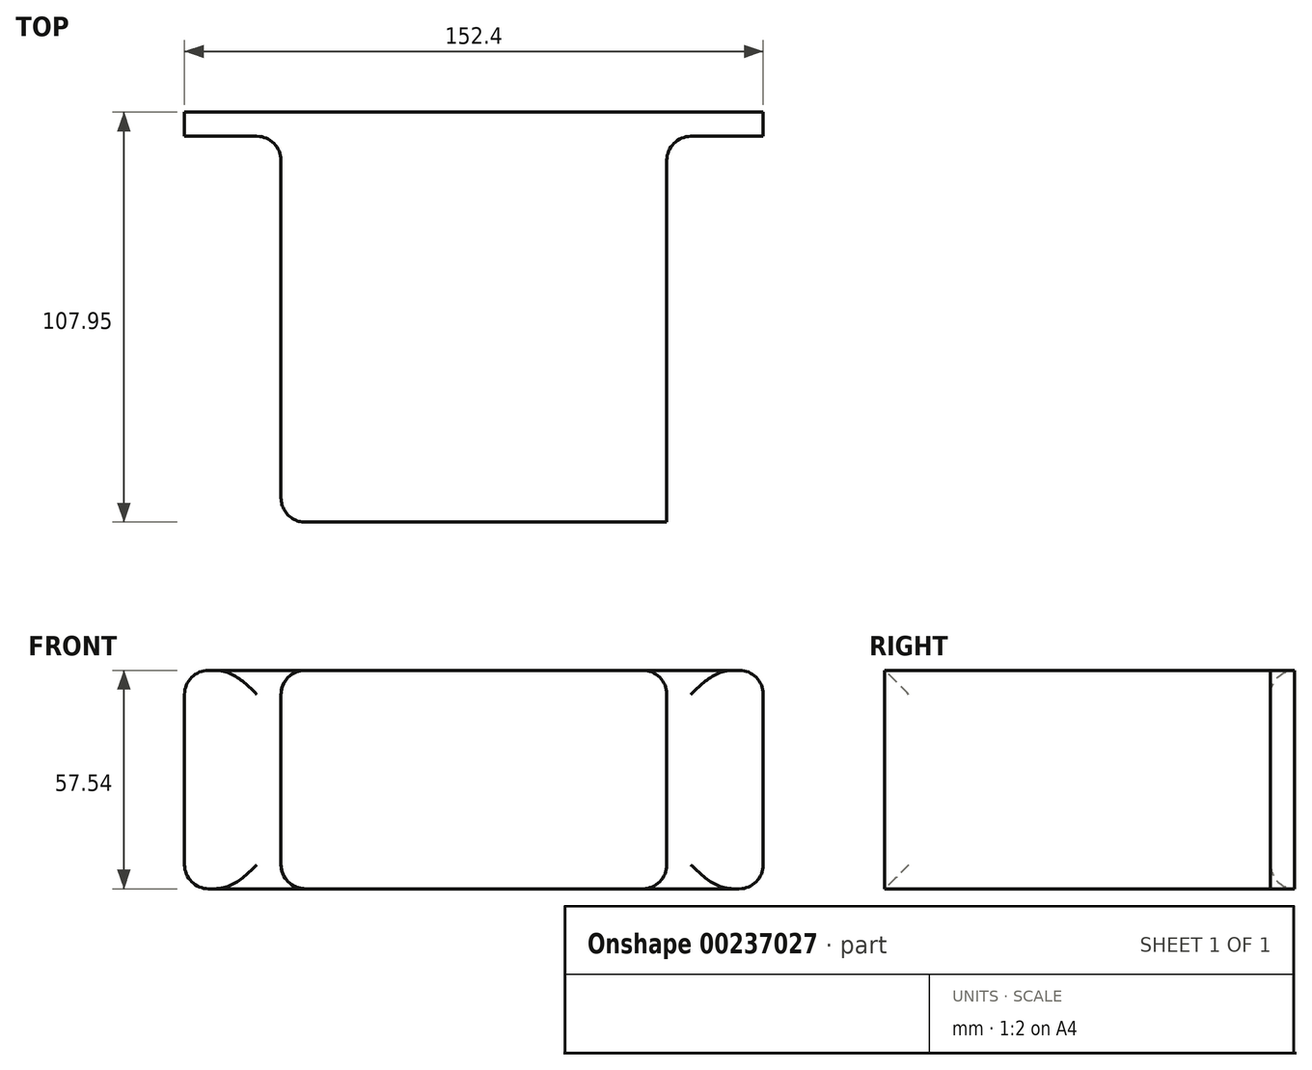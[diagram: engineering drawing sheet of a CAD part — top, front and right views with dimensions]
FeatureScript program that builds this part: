
annotation { "Feature Type Name" : "Feature", "Feature Type Description" : "" }
export const myFeature = defineFeature(function(context is Context, id is Id, definition is map)
    precondition{}
    {
        {
            var Q0;
            Q0=qCreatedBy(makeId("Front.planeOp"),FACE);
            var sketch = newSketch(context, id + "F0", { "sketchPlane" : qUnion([Q0])});
            skLineSegment(sketch, "E0.bottom", {"start": v(76.2, 28.77) * mm, "end": v(-76.2, 28.77) * mm});
            skLineSegment(sketch, "E0.top", {"start": v(76.2, -28.77) * mm, "end": v(-76.2, -28.77) * mm});
            skLineSegment(sketch, "E0.left", {"start": v(76.2, 28.77) * mm, "end": v(76.2, -28.77) * mm});
            skLineSegment(sketch, "E0.right", {"start": v(-76.2, 28.77) * mm, "end": v(-76.2, -28.77) * mm});
            skPoint(sketch, "E0.middle", {"position": v(0, 0) * mm});
            skSolve(sketch);
        }
        {
            var Q0;
            Q0=makeQuery(id+"F0.imprint","IMPRINT",FACE,{"disambiguationData":[TD([[makeQuery(id+"F0.imprint","IMPRINT",EDGE,{"derivedFrom":sQuery(id+"F0.wireOp",EDGE,"E0.bottom")}),1.0]])]});
            extrude(context, id + "F1", {"entities" : qUnion([Q0]), "depth" : 6.35 * mm});
        }
        {
            var Q0;
            Q0=makeQuery(id+"F1.opExtrude","CAP_FACE",FACE,{"disambiguationData":[OSD([sQuery(id+"F0.wireOp",EDGE,"E0.bottom"),sQuery(id+"F0.wireOp",EDGE,"E0.top"),sQuery(id+"F0.wireOp",EDGE,"E0.left"),sQuery(id+"F0.wireOp",EDGE,"E0.right")])],"isStart":false});
            var sketch = newSketch(context, id + "F2", { "sketchPlane" : qUnion([Q0])});
            skLineSegment(sketch, "E1.bottom", {"start": v(50.8, 28.77) * mm, "end": v(-50.8, 28.77) * mm});
            skLineSegment(sketch, "E1.top", {"start": v(50.8, -28.77) * mm, "end": v(-50.8, -28.77) * mm});
            skLineSegment(sketch, "E1.left", {"start": v(50.8, 28.77) * mm, "end": v(50.8, -28.77) * mm});
            skLineSegment(sketch, "E1.right", {"start": v(-50.8, 28.77) * mm, "end": v(-50.8, -28.77) * mm});
            skPoint(sketch, "E1.middle", {"position": v(0, 0) * mm});
            skSolve(sketch);
        }
        {
            var Q0;
            Q0 = qSketchRegion(id + "F2", true);
            extrude(context, id + "F3", {"entities" : qUnion([Q0]), "operationType" : NewBodyOperationType.ADD, "depth" : 101.6 * mm});
        }
        {
            var Q0;
            Q0=makeQuery(id+"F1.opExtrude","SWEPT_EDGE",EDGE,{"disambiguationData":[OSD([sQuery(id+"F0.wireOp",EDGE,"E0.top"),sQuery(id+"F0.wireOp",EDGE,"E0.right")])]});
            var Q1;
            Q1=makeQuery(id+"F3.opExtrude","SWEPT_EDGE",EDGE,{"disambiguationData":[OSD([sQuery(id+"F0.wireOp",EDGE,"E0.top"),sQuery(id+"F2.wireOp",EDGE,"E1.top"),sQuery(id+"F2.wireOp",EDGE,"E1.right")])]});
            var Q2;
            Q2=makeQuery(id+"F3.opExtrude","SWEPT_EDGE",EDGE,{"disambiguationData":[OSD([sQuery(id+"F0.wireOp",EDGE,"E0.bottom"),sQuery(id+"F2.wireOp",EDGE,"E1.bottom"),sQuery(id+"F2.wireOp",EDGE,"E1.right")])]});
            var Q3;
            Q3=makeQuery(id+"F3.opExtrude","SWEPT_EDGE",EDGE,{"disambiguationData":[OSD([sQuery(id+"F0.wireOp",EDGE,"E0.top"),sQuery(id+"F2.wireOp",EDGE,"E1.top"),sQuery(id+"F2.wireOp",EDGE,"E1.left")])]});
            var Q4;
            Q4=makeQuery(id+"F3.opExtrude","SWEPT_EDGE",EDGE,{"disambiguationData":[OSD([sQuery(id+"F0.wireOp",EDGE,"E0.bottom"),sQuery(id+"F2.wireOp",EDGE,"E1.bottom"),sQuery(id+"F2.wireOp",EDGE,"E1.left")])]});
            var Q5;
            Q5=makeQuery(id+"F3.opExtrude","CAP_EDGE",EDGE,{"disambiguationData":[OSD([sQuery(id+"F2.wireOp",EDGE,"E1.left")])],"isStart":true});
            var Q6;
            Q6=makeQuery(id+"F3.opExtrude","SWEPT_FACE",FACE,{"disambiguationData":[OSD([sQuery(id+"F2.wireOp",EDGE,"E1.right")])]});
            var Q7;
            Q7=makeQuery(id+"F1.opExtrude","SWEPT_EDGE",EDGE,{"disambiguationData":[OSD([sQuery(id+"F0.wireOp",EDGE,"E0.bottom"),sQuery(id+"F0.wireOp",EDGE,"E0.right")])]});
            var Q8;
            Q8=makeQuery(id+"F1.opExtrude","SWEPT_EDGE",EDGE,{"disambiguationData":[OSD([sQuery(id+"F0.wireOp",EDGE,"E0.bottom"),sQuery(id+"F0.wireOp",EDGE,"E0.left")])]});
            var Q9;
            Q9=makeQuery(id+"F1.opExtrude","SWEPT_EDGE",EDGE,{"disambiguationData":[OSD([sQuery(id+"F0.wireOp",EDGE,"E0.top"),sQuery(id+"F0.wireOp",EDGE,"E0.left")])]});
            fillet(context, id + "F4", {"entities" : qUnion([Q0, Q1, Q2, Q3, Q4, Q5, Q6, Q7, Q8, Q9]), "radius" : 6.35 * mm, "tangentPropagation" : true, "allowEdgeOverflow" : false});
        }
    });
